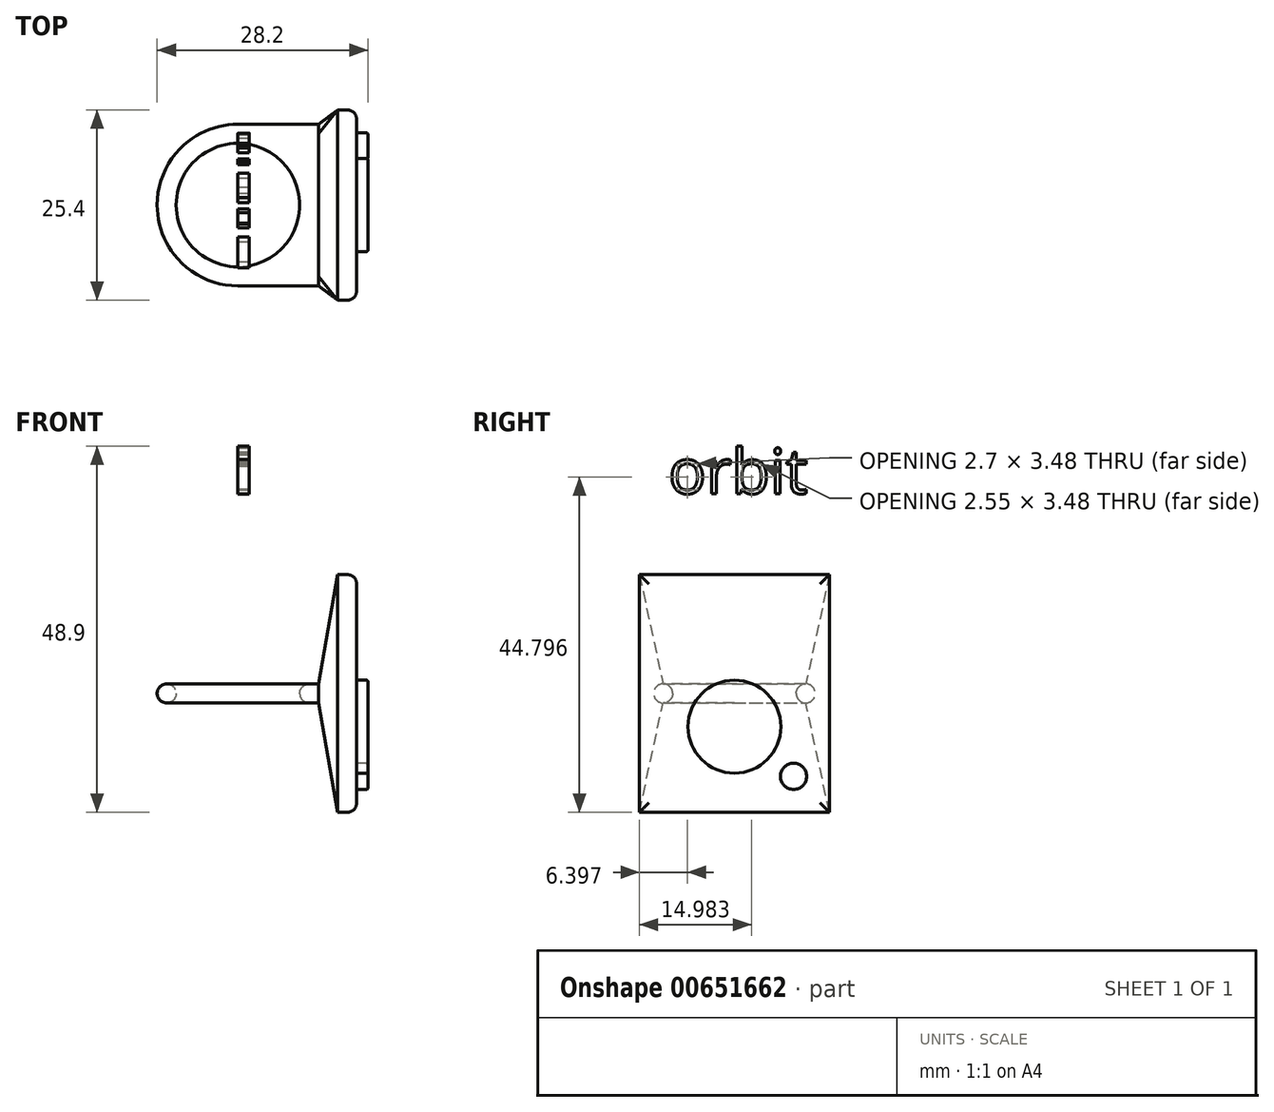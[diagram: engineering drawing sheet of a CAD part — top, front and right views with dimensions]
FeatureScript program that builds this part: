
annotation { "Feature Type Name" : "Feature", "Feature Type Description" : "" }
export const myFeature = defineFeature(function(context is Context, id is Id, definition is map)
    precondition{}
    {
        {
            var Q0;
            Q0=qCreatedBy(makeId("Top.planeOp"),FACE);
            var sketch = newSketch(context, id + "F0", { "sketchPlane" : qUnion([Q0])});
            skCircle(sketch, "E0", {"center": v(0, 0) * mm, "radius": 8.26 * mm});
            skCircle(sketch, "E1.0", {"center": v(0, 0) * mm, "radius": 10.8 * mm});
            skLineSegment(sketch, "E2", {"start": v(0, -10.8) * mm, "end": v(28.84, -10.8) * mm});
            skLineSegment(sketch, "E3", {"start": v(0, 10.8) * mm, "end": v(27.85, 10.8) * mm});
            skLineSegment(sketch, "E4", {"start": v(10.8, 0) * mm, "end": v(10.8, 10.8) * mm});
            skLineSegment(sketch, "E5", {"start": v(10.8, 10.8) * mm, "end": v(10.8, -10.8) * mm});
            skSolve(sketch);
        }
        {
            var Q0;
            Q0=qSketchRegion(id+"F0",true);
            extrude(context, id + "F1", {"entities" : qUnion([Q0]), "depth" : 2.54 * mm, "offsetDistance" : 25.4 * mm});
        }
        {
            var Q0;
            Q0=makeQuery(id+"F1.opExtrude","CAP_EDGE",EDGE,{"disambiguationData":[OSD([sQuery(id+"F0.wireOp",EDGE,"E0")])],"isStart":false});
            var Q1;
            Q1=makeQuery(id+"F1.opExtrude","CAP_EDGE",EDGE,{"disambiguationData":[OSD([sQuery(id+"F0.wireOp",EDGE,"E0")])],"isStart":true});
            var Q2;
            Q2=makeQuery(id+"F1.opExtrude","CAP_EDGE",EDGE,{"disambiguationData":[OSD([sQuery(id+"F0.wireOp",EDGE,"E1.0")])],"isStart":false});
            var Q3;
            Q3=makeQuery(id+"F1.opExtrude","CAP_EDGE",EDGE,{"disambiguationData":[OSD([sQuery(id+"F0.wireOp",EDGE,"E1.0")])],"isStart":true});
            fillet(context, id + "F2", {"entities" : qUnion([Q0, Q1, Q2, Q3]), "radius" : 1.27 * mm, "tangentPropagation" : true, "allowEdgeOverflow" : false});
        }
        {
            var Q0;
            Q0=makeQuery(id+"F1.opExtrude","SWEPT_FACE",FACE,{"disambiguationData":[OSD([sQuery(id+"F0.wireOp",EDGE,"E5")])]});
            cPlane(context, id + "F3", {"entities" : qUnion([Q0]), "cplaneType" : CPlaneType.OFFSET, "offset" : 2.54 * mm, "width" : 152.4 * mm, "height" : 152.4 * mm});
        }
        {
            var Q0;
            Q0=qCreatedBy(id+"F3.planeOp",FACE);
            var sketch = newSketch(context, id + "F4", { "sketchPlane" : qUnion([Q0])});
            skLineSegment(sketch, "E6", {"start": v(0, 0) * mm, "end": v(0, 2.54) * mm});
            skLineSegment(sketch, "E7.bottom", {"start": v(-12.7, 17.15) * mm, "end": v(12.7, 17.15) * mm});
            skLineSegment(sketch, "E7.top", {"start": v(-12.7, -14.6) * mm, "end": v(12.7, -14.6) * mm});
            skLineSegment(sketch, "E7.left", {"start": v(-12.7, 17.15) * mm, "end": v(-12.7, -14.6) * mm});
            skLineSegment(sketch, "E7.right", {"start": v(12.7, 17.15) * mm, "end": v(12.7, -14.6) * mm});
            skPoint(sketch, "E7.middle", {"position": v(0, 1.27) * mm});
            skSolve(sketch);
        }
        {
            var Q0;
            Q0=qSketchRegion(id+"F4",true);
            extrude(context, id + "F5", {"entities" : qUnion([Q0]), "depth" : 2.54 * mm, "offsetDistance" : 25.4 * mm});
        }
        {
            var Q0;
            Q0=makeQuery(id+"F5.opExtrude","CAP_FACE",FACE,{"disambiguationData":[OSD([sQuery(id+"F4.wireOp",EDGE,"E7.bottom"),sQuery(id+"F4.wireOp",EDGE,"E7.top"),sQuery(id+"F4.wireOp",EDGE,"E7.left"),sQuery(id+"F4.wireOp",EDGE,"E7.right")])],"isStart":true});
            var Q1;
            Q1=makeQuery(id+"F1.opExtrude","SWEPT_FACE",FACE,{"disambiguationData":[OSD([sQuery(id+"F0.wireOp",EDGE,"E5")])]});
            loft(context, id + "F6", {"sheetProfilesArray" : [{ "sheetProfileEntities" : qUnion([Q0]) }, { "sheetProfileEntities" : qUnion([Q1]) }]});
        }
        {
            var Q0;
            Q0=makeQuery(id+"F5.opExtrude","CAP_EDGE",EDGE,{"disambiguationData":[OSD([sQuery(id+"F4.wireOp",EDGE,"E7.right")])],"isStart":false});
            var Q1;
            Q1=makeQuery(id+"F5.opExtrude","CAP_EDGE",EDGE,{"disambiguationData":[OSD([sQuery(id+"F4.wireOp",EDGE,"E7.bottom")])],"isStart":false});
            var Q2;
            Q2=makeQuery(id+"F5.opExtrude","CAP_EDGE",EDGE,{"disambiguationData":[OSD([sQuery(id+"F4.wireOp",EDGE,"E7.top")])],"isStart":false});
            var Q3;
            Q3=makeQuery(id+"F5.opExtrude","CAP_EDGE",EDGE,{"disambiguationData":[OSD([sQuery(id+"F4.wireOp",EDGE,"E7.left")])],"isStart":false});
            fillet(context, id + "F7", {"entities" : qUnion([Q0, Q1, Q2, Q3]), "radius" : 1.27 * mm, "tangentPropagation" : true, "allowEdgeOverflow" : false});
        }
        {
            var Q0;
            Q0=makeQuery(id+"F5.opExtrude","CAP_FACE",FACE,{"disambiguationData":[OSD([sQuery(id+"F4.wireOp",EDGE,"E7.bottom"),sQuery(id+"F4.wireOp",EDGE,"E7.top"),sQuery(id+"F4.wireOp",EDGE,"E7.left"),sQuery(id+"F4.wireOp",EDGE,"E7.right")])],"isStart":false});
            var sketch = newSketch(context, id + "F8", { "sketchPlane" : qUnion([Q0])});
            skLineSegment(sketch, "E8", {"start": v(0, -13.34) * mm, "end": v(0, 15.88) * mm});
            skCircle(sketch, "E9", {"center": v(0, -3.17) * mm, "radius": 6.2 * mm});
            skCircle(sketch, "E10", {"center": v(7.9, -9.8) * mm, "radius": 1.75 * mm});
            skSolve(sketch);
        }
        {
            var Q0;
            Q0=qSketchRegion(id+"F8",true);
            extrude(context, id + "F9", {"entities" : qUnion([Q0]), "operationType" : NewBodyOperationType.ADD, "depth" : 1.52 * mm, "offsetDistance" : 25.4 * mm});
        }
        {
            var Q0;
            Q0=makeQuery(id+"F9.opExtrude","CAP_FACE",FACE,{"disambiguationData":[OSD([sQuery(id+"F8.wireOp",EDGE,"E9")])],"isStart":false});
            var Q1;
            Q1=makeQuery(id+"F9.opExtrude","CAP_FACE",FACE,{"disambiguationData":[OSD([sQuery(id+"F8.wireOp",EDGE,"cirWsNv0-ULYx-fZ3N-6p8o-yrHtWYinyU7r")])],"isStart":false});
            var Q2;
            Q2=makeQuery(id+"F9.opExtrude","CAP_FACE",FACE,{"disambiguationData":[OSD([sQuery(id+"F8.wireOp",EDGE,"E10")])],"isStart":false});
            fillet(context, id + "F10", {"entities" : qUnion([Q0, Q1, Q2]), "radius" : 0.25 * mm, "tangentPropagation" : true, "allowEdgeOverflow" : false});
        }
        {
            var Q0;
            Q0=qCreatedBy(makeId("Right.planeOp"),FACE);
            var sketch = newSketch(context, id + "F11", { "sketchPlane" : qUnion([Q0])});
            skText(sketch, "E11", { "text": "orbit", "fontName": "OpenSans-Regular.ttf"});
            const initialGuessF11  = {"E11": [-0.00735, 0.0233, 1, 0, 0.005]};
            skSetInitialGuess(sketch, initialGuessF11);
            skSolve(sketch);
        }
        {
            var Q0;
            Q0 = qSketchRegion(id + "F11", true);
            extrude(context, id + "F12", {"entities" : qUnion([Q0]), "depth" : 1.27 * mm, "offsetDistance" : 25.4 * mm});
        }
        {
            var Q0;
            Q0=makeQuery(id+"F12.opExtrude","SWEPT_BODY",BODY,{"disambiguationData":[OSD([sQuery(id+"F11.wireOp",EDGE,"E11.sketch_text.stroke-0"),sQuery(id+"F11.wireOp",EDGE,"E11.sketch_text.stroke-1"),sQuery(id+"F11.wireOp",EDGE,"E11.sketch_text.stroke-2"),sQuery(id+"F11.wireOp",EDGE,"E11.sketch_text.stroke-3"),sQuery(id+"F11.wireOp",EDGE,"E11.sketch_text.stroke-4"),sQuery(id+"F11.wireOp",EDGE,"E11.sketch_text.stroke-5"),sQuery(id+"F11.wireOp",EDGE,"E11.sketch_text.stroke-6"),sQuery(id+"F11.wireOp",EDGE,"E11.sketch_text.stroke-7"),sQuery(id+"F11.wireOp",EDGE,"E11.sketch_text.stroke-8"),sQuery(id+"F11.wireOp",EDGE,"E11.sketch_text.stroke-9"),sQuery(id+"F11.wireOp",EDGE,"E11.sketch_text.stroke-10"),sQuery(id+"F11.wireOp",EDGE,"E11.sketch_text.stroke-11"),sQuery(id+"F11.wireOp",EDGE,"E11.sketch_text.stroke-12"),sQuery(id+"F11.wireOp",EDGE,"E11.sketch_text.stroke-13"),sQuery(id+"F11.wireOp",EDGE,"E11.sketch_text.stroke-14"),sQuery(id+"F11.wireOp",EDGE,"E11.sketch_text.stroke-15"),sQuery(id+"F11.wireOp",EDGE,"E11.sketch_text.stroke-16")])]});
            var Q1;
            Q1=makeQuery(id+"F12.opExtrude","SWEPT_BODY",BODY,{"disambiguationData":[OSD([sQuery(id+"F11.wireOp",EDGE,"E11.sketch_text.stroke-17"),sQuery(id+"F11.wireOp",EDGE,"E11.sketch_text.stroke-18"),sQuery(id+"F11.wireOp",EDGE,"E11.sketch_text.stroke-19"),sQuery(id+"F11.wireOp",EDGE,"E11.sketch_text.stroke-20"),sQuery(id+"F11.wireOp",EDGE,"E11.sketch_text.stroke-21"),sQuery(id+"F11.wireOp",EDGE,"E11.sketch_text.stroke-22"),sQuery(id+"F11.wireOp",EDGE,"E11.sketch_text.stroke-23"),sQuery(id+"F11.wireOp",EDGE,"E11.sketch_text.stroke-24"),sQuery(id+"F11.wireOp",EDGE,"E11.sketch_text.stroke-25"),sQuery(id+"F11.wireOp",EDGE,"E11.sketch_text.stroke-26"),sQuery(id+"F11.wireOp",EDGE,"E11.sketch_text.stroke-27"),sQuery(id+"F11.wireOp",EDGE,"E11.sketch_text.stroke-28"),sQuery(id+"F11.wireOp",EDGE,"E11.sketch_text.stroke-29")])]});
            var Q2;
            Q2=makeQuery(id+"F12.opExtrude","SWEPT_BODY",BODY,{"disambiguationData":[OSD([sQuery(id+"F11.wireOp",EDGE,"E11.sketch_text.stroke-30"),sQuery(id+"F11.wireOp",EDGE,"E11.sketch_text.stroke-31"),sQuery(id+"F11.wireOp",EDGE,"E11.sketch_text.stroke-32"),sQuery(id+"F11.wireOp",EDGE,"E11.sketch_text.stroke-33"),sQuery(id+"F11.wireOp",EDGE,"E11.sketch_text.stroke-34"),sQuery(id+"F11.wireOp",EDGE,"E11.sketch_text.stroke-35"),sQuery(id+"F11.wireOp",EDGE,"E11.sketch_text.stroke-36"),sQuery(id+"F11.wireOp",EDGE,"E11.sketch_text.stroke-37"),sQuery(id+"F11.wireOp",EDGE,"E11.sketch_text.stroke-38"),sQuery(id+"F11.wireOp",EDGE,"E11.sketch_text.stroke-39"),sQuery(id+"F11.wireOp",EDGE,"E11.sketch_text.stroke-40"),sQuery(id+"F11.wireOp",EDGE,"E11.sketch_text.stroke-41"),sQuery(id+"F11.wireOp",EDGE,"E11.sketch_text.stroke-42"),sQuery(id+"F11.wireOp",EDGE,"E11.sketch_text.stroke-43"),sQuery(id+"F11.wireOp",EDGE,"E11.sketch_text.stroke-44"),sQuery(id+"F11.wireOp",EDGE,"E11.sketch_text.stroke-45"),sQuery(id+"F11.wireOp",EDGE,"E11.sketch_text.stroke-46"),sQuery(id+"F11.wireOp",EDGE,"E11.sketch_text.stroke-47"),sQuery(id+"F11.wireOp",EDGE,"E11.sketch_text.stroke-48"),sQuery(id+"F11.wireOp",EDGE,"E11.sketch_text.stroke-49"),sQuery(id+"F11.wireOp",EDGE,"E11.sketch_text.stroke-50"),sQuery(id+"F11.wireOp",EDGE,"E11.sketch_text.stroke-51"),sQuery(id+"F11.wireOp",EDGE,"E11.sketch_text.stroke-52")])]});
            var Q3;
            Q3=makeQuery(id+"F12.opExtrude","SWEPT_BODY",BODY,{"disambiguationData":[OSD([sQuery(id+"F11.wireOp",EDGE,"E11.sketch_text.stroke-53"),sQuery(id+"F11.wireOp",EDGE,"E11.sketch_text.stroke-54"),sQuery(id+"F11.wireOp",EDGE,"E11.sketch_text.stroke-55"),sQuery(id+"F11.wireOp",EDGE,"E11.sketch_text.stroke-56")])]});
            var Q4;
            Q4=makeQuery(id+"F12.opExtrude","SWEPT_BODY",BODY,{"disambiguationData":[OSD([sQuery(id+"F11.wireOp",EDGE,"E11.sketch_text.stroke-57"),sQuery(id+"F11.wireOp",EDGE,"E11.sketch_text.stroke-58"),sQuery(id+"F11.wireOp",EDGE,"E11.sketch_text.stroke-59"),sQuery(id+"F11.wireOp",EDGE,"E11.sketch_text.stroke-60"),sQuery(id+"F11.wireOp",EDGE,"E11.sketch_text.stroke-61"),sQuery(id+"F11.wireOp",EDGE,"E11.sketch_text.stroke-62"),sQuery(id+"F11.wireOp",EDGE,"E11.sketch_text.stroke-63"),sQuery(id+"F11.wireOp",EDGE,"E11.sketch_text.stroke-64")])]});
            var Q5;
            Q5=makeQuery(id+"F12.opExtrude","SWEPT_BODY",BODY,{"disambiguationData":[OSD([sQuery(id+"F11.wireOp",EDGE,"E11.sketch_text.stroke-65"),sQuery(id+"F11.wireOp",EDGE,"E11.sketch_text.stroke-66"),sQuery(id+"F11.wireOp",EDGE,"E11.sketch_text.stroke-67"),sQuery(id+"F11.wireOp",EDGE,"E11.sketch_text.stroke-68"),sQuery(id+"F11.wireOp",EDGE,"E11.sketch_text.stroke-69"),sQuery(id+"F11.wireOp",EDGE,"E11.sketch_text.stroke-70"),sQuery(id+"F11.wireOp",EDGE,"E11.sketch_text.stroke-71"),sQuery(id+"F11.wireOp",EDGE,"E11.sketch_text.stroke-72"),sQuery(id+"F11.wireOp",EDGE,"E11.sketch_text.stroke-73"),sQuery(id+"F11.wireOp",EDGE,"E11.sketch_text.stroke-74"),sQuery(id+"F11.wireOp",EDGE,"E11.sketch_text.stroke-75"),sQuery(id+"F11.wireOp",EDGE,"E11.sketch_text.stroke-76"),sQuery(id+"F11.wireOp",EDGE,"E11.sketch_text.stroke-77"),sQuery(id+"F11.wireOp",EDGE,"E11.sketch_text.stroke-78"),sQuery(id+"F11.wireOp",EDGE,"E11.sketch_text.stroke-79"),sQuery(id+"F11.wireOp",EDGE,"E11.sketch_text.stroke-80"),sQuery(id+"F11.wireOp",EDGE,"E11.sketch_text.stroke-81"),sQuery(id+"F11.wireOp",EDGE,"E11.sketch_text.stroke-82"),sQuery(id+"F11.wireOp",EDGE,"E11.sketch_text.stroke-83")])]});
            var Q6;
            Q6=qCreatedBy(makeId("Origin.pointOp"),VERTEX);
            transform(context, id + "F13", {"entities" : qUnion([Q0, Q1, Q2, Q3, Q4, Q5]), "transformType" : TransformType.SCALE_UNIFORMLY, "scale" : 1.2, "scalePoint" : qUnion([Q6]), "makeCopy" : false});
        }
    });
